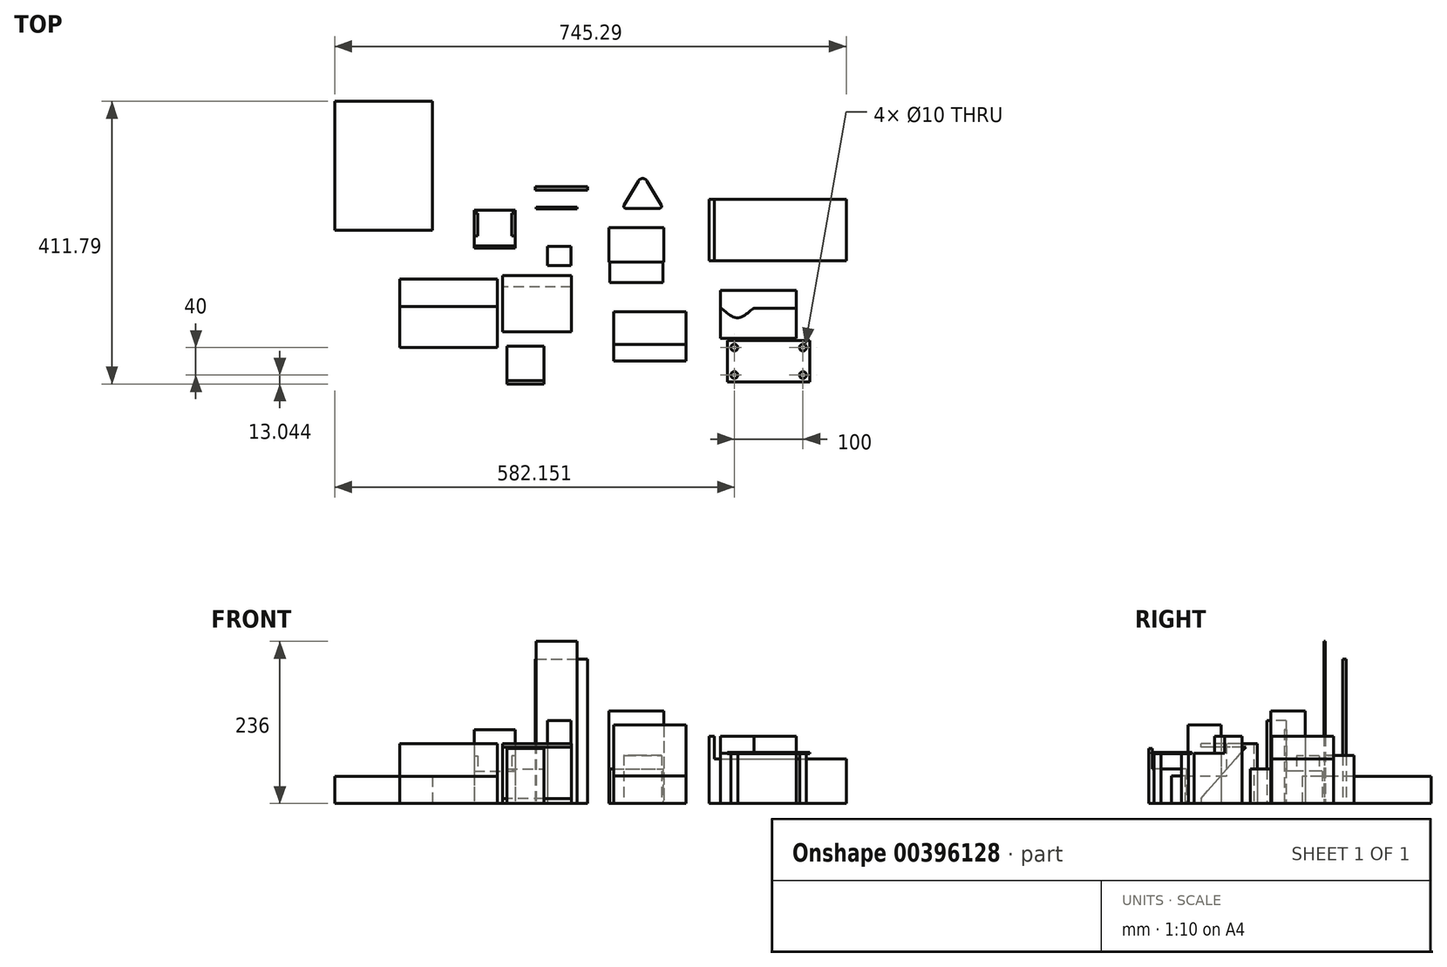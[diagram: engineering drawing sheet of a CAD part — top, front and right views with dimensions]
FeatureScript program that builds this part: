
annotation { "Feature Type Name" : "Feature", "Feature Type Description" : "" }
export const myFeature = defineFeature(function(context is Context, id is Id, definition is map)
    precondition{}
    {
        {
            var Q0;
            Q0=qCreatedBy(makeId("Top.planeOp"),FACE);
            var sketch = newSketch(context, id + "F0", { "sketchPlane" : qUnion([Q0])});
            skLineSegment(sketch, "E0.bottom", {"start": v(-111.36, 82.37) * mm, "end": v(-31.36, 82.37) * mm});
            skLineSegment(sketch, "E0.top", {"start": v(-111.36, 32.37) * mm, "end": v(-31.36, 32.37) * mm});
            skLineSegment(sketch, "E0.left", {"start": v(-111.36, 82.37) * mm, "end": v(-111.36, 32.37) * mm});
            skLineSegment(sketch, "E0.right", {"start": v(-31.36, 82.37) * mm, "end": v(-31.36, 32.37) * mm});
            skLineSegment(sketch, "E1.bottom", {"start": v(34.65, 123.83) * mm, "end": v(234.65, 123.83) * mm});
            skLineSegment(sketch, "E1.top", {"start": v(34.65, 33.83) * mm, "end": v(234.65, 33.83) * mm});
            skLineSegment(sketch, "E1.left", {"start": v(34.65, 123.83) * mm, "end": v(34.65, 33.83) * mm});
            skLineSegment(sketch, "E1.right", {"start": v(234.65, 123.83) * mm, "end": v(234.65, 33.83) * mm});
            skLineSegment(sketch, "E2.bottom", {"start": v(-104.09, -40.21) * mm, "end": v(0.91, -40.21) * mm});
            skLineSegment(sketch, "E2.top", {"start": v(-104.09, -88.21) * mm, "end": v(0.91, -88.21) * mm});
            skLineSegment(sketch, "E2.left", {"start": v(-104.09, -40.21) * mm, "end": v(-104.09, -88.21) * mm});
            skLineSegment(sketch, "E2.right", {"start": v(0.91, -40.21) * mm, "end": v(0.91, -88.21) * mm});
            skLineSegment(sketch, "E3.bottom", {"start": v(51.44, -9.18) * mm, "end": v(161.44, -9.18) * mm});
            skLineSegment(sketch, "E3.top", {"start": v(51.44, -79.18) * mm, "end": v(161.44, -79.18) * mm});
            skLineSegment(sketch, "E3.left", {"start": v(51.44, -9.18) * mm, "end": v(51.44, -79.18) * mm});
            skLineSegment(sketch, "E3.right", {"start": v(161.44, -9.18) * mm, "end": v(161.44, -79.18) * mm});
            skLineSegment(sketch, "E4.bottom", {"start": v(-110.36, 32.37) * mm, "end": v(-32.36, 32.37) * mm});
            skLineSegment(sketch, "E4.top", {"start": v(-110.36, 2.37) * mm, "end": v(-32.36, 2.37) * mm});
            skLineSegment(sketch, "E4.left", {"start": v(-110.36, 32.37) * mm, "end": v(-110.36, 2.37) * mm});
            skLineSegment(sketch, "E4.right", {"start": v(-32.36, 32.37) * mm, "end": v(-32.36, 2.37) * mm});
            skPoint(sketch, "E5", {"position": v(-71.36, 32.37) * mm});
            skPoint(sketch, "E6", {"position": v(-71.36, 2.37) * mm});
            skLineSegment(sketch, "E7", {"start": v(42.4, 123.83) * mm, "end": v(42.4, 33.83) * mm});
            skLineSegment(sketch, "E8.bottom", {"start": v(61.51, -82.45) * mm, "end": v(181.51, -82.45) * mm});
            skLineSegment(sketch, "E8.top", {"start": v(61.51, -142.45) * mm, "end": v(181.51, -142.45) * mm});
            skLineSegment(sketch, "E8.left", {"start": v(61.51, -82.45) * mm, "end": v(61.51, -142.45) * mm});
            skLineSegment(sketch, "E8.right", {"start": v(181.51, -82.45) * mm, "end": v(181.51, -142.45) * mm});
            skCircle(sketch, "E9", {"center": v(71.51, -92.45) * mm, "radius": 5 * mm});
            skCircle(sketch, "E10", {"center": v(71.51, -132.45) * mm, "radius": 5 * mm});
            skCircle(sketch, "E11", {"center": v(171.51, -92.45) * mm, "radius": 5 * mm});
            skCircle(sketch, "E12", {"center": v(171.51, -132.45) * mm, "radius": 5 * mm});
            skLineSegment(sketch, "E13.bottom", {"start": v(-200.88, 54.96) * mm, "end": v(-166.38, 54.96) * mm});
            skLineSegment(sketch, "E13.top", {"start": v(-200.88, 26.96) * mm, "end": v(-166.38, 26.96) * mm});
            skLineSegment(sketch, "E13.left", {"start": v(-200.88, 54.96) * mm, "end": v(-200.88, 26.96) * mm});
            skLineSegment(sketch, "E13.right", {"start": v(-166.38, 54.96) * mm, "end": v(-166.38, 26.96) * mm});
            skLineSegment(sketch, "E14.bottom", {"start": v(-266.16, 12.56) * mm, "end": v(-166.16, 12.56) * mm});
            skLineSegment(sketch, "E14.top", {"start": v(-266.16, -69.44) * mm, "end": v(-166.16, -69.44) * mm});
            skLineSegment(sketch, "E14.left", {"start": v(-266.16, 12.56) * mm, "end": v(-266.16, -69.44) * mm});
            skLineSegment(sketch, "E14.right", {"start": v(-166.16, 12.56) * mm, "end": v(-166.16, -69.44) * mm});
            skLineSegment(sketch, "E15.bottom", {"start": v(-218.52, 142.09) * mm, "end": v(-142.52, 142.09) * mm});
            skLineSegment(sketch, "E15.top", {"start": v(-218.52, 137.09) * mm, "end": v(-142.52, 137.09) * mm});
            skLineSegment(sketch, "E15.left", {"start": v(-218.52, 142.09) * mm, "end": v(-218.52, 137.09) * mm});
            skLineSegment(sketch, "E15.right", {"start": v(-142.52, 142.09) * mm, "end": v(-142.52, 137.09) * mm});
            skLineSegment(sketch, "E16.bottom", {"start": v(-217.4, 111.88) * mm, "end": v(-157.4, 111.88) * mm});
            skLineSegment(sketch, "E16.top", {"start": v(-217.4, 109.88) * mm, "end": v(-157.4, 109.88) * mm});
            skLineSegment(sketch, "E16.left", {"start": v(-217.4, 111.88) * mm, "end": v(-217.4, 109.88) * mm});
            skLineSegment(sketch, "E16.right", {"start": v(-157.4, 111.88) * mm, "end": v(-157.4, 109.88) * mm});
            skLineSegment(sketch, "E17.top", {"start": v(-104.09, -112.21) * mm, "end": v(0.91, -112.21) * mm});
            skLineSegment(sketch, "E17.left", {"start": v(-104.09, -88.21) * mm, "end": v(-104.09, -112.21) * mm});
            skLineSegment(sketch, "E17.right", {"start": v(0.91, -88.21) * mm, "end": v(0.91, -112.21) * mm});
            skLineSegment(sketch, "E18.bottom", {"start": v(-307.61, 107.39) * mm, "end": v(-247.61, 107.39) * mm});
            skLineSegment(sketch, "E18.top", {"start": v(-307.61, 52.39) * mm, "end": v(-247.61, 52.39) * mm});
            skLineSegment(sketch, "E18.left", {"start": v(-307.61, 107.39) * mm, "end": v(-307.61, 52.39) * mm});
            skLineSegment(sketch, "E18.right", {"start": v(-247.61, 107.39) * mm, "end": v(-247.61, 52.39) * mm});
            skLineSegment(sketch, "E19.bottom", {"start": v(-259.82, -90.49) * mm, "end": v(-205.82, -90.49) * mm});
            skLineSegment(sketch, "E19.top", {"start": v(-259.82, -145.49) * mm, "end": v(-205.82, -145.49) * mm});
            skLineSegment(sketch, "E19.left", {"start": v(-259.82, -90.49) * mm, "end": v(-259.82, -145.49) * mm});
            skLineSegment(sketch, "E19.right", {"start": v(-205.82, -90.49) * mm, "end": v(-205.82, -145.49) * mm});
            skLineSegment(sketch, "E20", {"start": v(-62.11, 160.46) * mm, "end": v(-92.11, 110.46) * mm});
            skLineSegment(sketch, "E21", {"start": v(-92.11, 110.46) * mm, "end": v(-32.11, 110.46) * mm});
            skLineSegment(sketch, "E22", {"start": v(-32.11, 110.46) * mm, "end": v(-62.11, 160.46) * mm});
            skPoint(sketch, "E23", {"position": v(-62.11, 110.46) * mm});
            skLineSegment(sketch, "E24.bottom", {"start": v(-415.9, 7.38) * mm, "end": v(-273.9, 7.38) * mm});
            skLineSegment(sketch, "E24.top", {"start": v(-415.9, -92.62) * mm, "end": v(-273.9, -92.62) * mm});
            skLineSegment(sketch, "E24.left", {"start": v(-415.9, 7.38) * mm, "end": v(-415.9, -92.62) * mm});
            skLineSegment(sketch, "E24.right", {"start": v(-273.9, 7.38) * mm, "end": v(-273.9, -92.62) * mm});
            skLineSegment(sketch, "E25.bottom", {"start": v(-510.64, 266.3) * mm, "end": v(-368.64, 266.3) * mm});
            skLineSegment(sketch, "E25.top", {"start": v(-510.64, 78.3) * mm, "end": v(-368.64, 78.3) * mm});
            skLineSegment(sketch, "E25.left", {"start": v(-510.64, 266.3) * mm, "end": v(-510.64, 78.3) * mm});
            skLineSegment(sketch, "E25.right", {"start": v(-368.64, 266.3) * mm, "end": v(-368.64, 78.3) * mm});
            skLineSegment(sketch, "E26.top", {"start": v(-415.9, -32.62) * mm, "end": v(-273.9, -32.62) * mm});
            skLineSegment(sketch, "E26.left", {"start": v(-415.9, 7.38) * mm, "end": v(-415.9, -32.62) * mm});
            skLineSegment(sketch, "E26.right", {"start": v(-273.9, 7.38) * mm, "end": v(-273.9, -32.62) * mm});
            skSolve(sketch);
        }
        {
            var Q0;
            Q0=makeQuery(id+"F0.imprint","IMPRINT",FACE,{"disambiguationData":[TD([[makeQuery(id+"F0.imprint","IMPRINT",EDGE,{"derivedFrom":sQuery(id+"F0.wireOp",EDGE,"E0.bottom")}),-1.0]])]});
            extrude(context, id + "F1", {"entities" : qUnion([Q0]), "depth" : 134.5 * mm});
        }
        {
            var Q0;
            Q0=makeQuery(id+"F0.imprint","IMPRINT",FACE,{"disambiguationData":[TD([[makeQuery(id+"F0.imprint","IMPRINT",EDGE,{"derivedFrom":sQuery(id+"F0.wireOp",EDGE,"E4.top")}),1.0]])]});
            extrude(context, id + "F2", {"entities" : qUnion([Q0]), "operationType" : NewBodyOperationType.ADD, "depth" : 50 * mm});
        }
        {
            var Q0;
            {var subQ2=sQuery(id+"F0.wireOp",EDGE,"E1.right");Q0=makeQuery(id+"F0.imprint","IMPRINT",FACE,{"disambiguationData":[TD([[makeQuery(id+"F0.imprint","IMPRINT",EDGE,{"derivedFrom":subQ2}),-1.0]])]});}
            extrude(context, id + "F3", {"entities" : qUnion([Q0]), "depth" : 65 * mm});
        }
        {
            var Q0;
            {var subQ2=sQuery(id+"F0.wireOp",EDGE,"E1.left");Q0=makeQuery(id+"F0.imprint","IMPRINT",FACE,{"disambiguationData":[TD([[makeQuery(id+"F0.imprint","IMPRINT",EDGE,{"derivedFrom":subQ2}),1.0]])]});}
            extrude(context, id + "F4", {"entities" : qUnion([Q0]), "operationType" : NewBodyOperationType.ADD, "depth" : 98 * mm});
        }
        {
            var Q0;
            Q0=makeQuery(id+"F0.imprint","IMPRINT",FACE,{"disambiguationData":[TD([[makeQuery(id+"F0.imprint","IMPRINT",EDGE,{"derivedFrom":sQuery(id+"F0.wireOp",EDGE,"E3.bottom")}),-1.0]])]});
            extrude(context, id + "F5", {"entities" : qUnion([Q0]), "depth" : 73 * mm});
        }
        {
            var Q0;
            Q0=makeQuery(id+"F0.imprint","IMPRINT",FACE,{"disambiguationData":[TD([[makeQuery(id+"F0.imprint","IMPRINT",EDGE,{"derivedFrom":sQuery(id+"F0.wireOp",EDGE,"E2.bottom")}),-1.0]])]});
            extrude(context, id + "F6", {"entities" : qUnion([Q0]), "depth" : 114 * mm});
        }
        {
            var Q0;
            Q0=makeQuery(id+"F5.opExtrude","CAP_FACE",FACE,{"disambiguationData":[OSD([sQuery(id+"F0.wireOp",EDGE,"E3.bottom"),sQuery(id+"F0.wireOp",EDGE,"E3.top"),sQuery(id+"F0.wireOp",EDGE,"E3.left"),sQuery(id+"F0.wireOp",EDGE,"E3.right")])],"isStart":false});
            var sketch = newSketch(context, id + "F7", { "sketchPlane" : qUnion([Q0])});
            skLineSegment(sketch, "E27", {"start": v(161.44, -35.18) * mm, "end": v(100.44, -35.18) * mm});
            skFitSpline(sketch, "E28", {"points": [v(100.44, -35.18) * mm, v(75.94, -49.18) * mm, v(51.44, -35.18) * mm], "startDerivative": vector(-35.13, -15.5) * mm, "endDerivative": vector(-34.5, 15.56) * mm});
            skSolve(sketch);
        }
        {
            var Q0;
            {var subQ3=sQuery(id+"F7.wireOp",EDGE,"E27");Q0=makeQuery(id+"F7.imprint","IMPRINT",FACE,{"disambiguationData":[TD([[makeQuery(id+"F7.imprint","IMPRINT",EDGE,{"derivedFrom":subQ3}),-1.0]])]});}
            extrude(context, id + "F8", {"entities" : qUnion([Q0]), "operationType" : NewBodyOperationType.ADD, "depth" : 25 * mm});
        }
        {
            var Q0;
            Q0=makeQuery(id+"F0.imprint","IMPRINT",FACE,{"disambiguationData":[TD([[makeQuery(id+"F0.imprint","IMPRINT",EDGE,{"derivedFrom":sQuery(id+"F0.wireOp",EDGE,"E9")}),1.0]])]});
            var Q1;
            Q1=makeQuery(id+"F0.imprint","IMPRINT",FACE,{"disambiguationData":[TD([[makeQuery(id+"F0.imprint","IMPRINT",EDGE,{"derivedFrom":sQuery(id+"F0.wireOp",EDGE,"E11")}),1.0]])]});
            var Q2;
            Q2=makeQuery(id+"F0.imprint","IMPRINT",FACE,{"disambiguationData":[TD([[makeQuery(id+"F0.imprint","IMPRINT",EDGE,{"derivedFrom":sQuery(id+"F0.wireOp",EDGE,"E12")}),1.0]])]});
            var Q3;
            Q3=makeQuery(id+"F0.imprint","IMPRINT",FACE,{"disambiguationData":[TD([[makeQuery(id+"F0.imprint","IMPRINT",EDGE,{"derivedFrom":sQuery(id+"F0.wireOp",EDGE,"E10")}),1.0]])]});
            extrude(context, id + "F9", {"entities" : qUnion([Q0, Q1, Q2, Q3]), "depth" : 74 * mm});
        }
        {
            var Q0;
            Q0=makeQuery(id+"F0.imprint","IMPRINT",FACE,{"disambiguationData":[TD([[makeQuery(id+"F0.imprint","IMPRINT",EDGE,{"derivedFrom":sQuery(id+"F0.wireOp",EDGE,"E8.bottom")}),-1.0]])]});
            extrude(context, id + "F10", {"entities" : qUnion([Q0]), "depth" : 74 * mm, "hasSecondDirection" : true, "secondDirectionOppositeDirection" : false, "secondDirectionDepth" : 72 * mm});
        }
        {
            var Q0;
            Q0=makeQuery(id+"F0.imprint","IMPRINT",FACE,{"disambiguationData":[TD([[makeQuery(id+"F0.imprint","IMPRINT",EDGE,{"derivedFrom":sQuery(id+"F0.wireOp",EDGE,"E13.bottom")}),-1.0]])]});
            extrude(context, id + "F11", {"entities" : qUnion([Q0]), "depth" : 120.5 * mm, "offsetDistance" : 25 * mm});
        }
        {
            var Q0;
            Q0=makeQuery(id+"F0.imprint","IMPRINT",FACE,{"disambiguationData":[TD([[makeQuery(id+"F0.imprint","IMPRINT",EDGE,{"derivedFrom":sQuery(id+"F0.wireOp",EDGE,"E14.bottom")}),-1.0]])]});
            extrude(context, id + "F12", {"entities" : qUnion([Q0]), "depth" : 87 * mm, "offsetDistance" : 25 * mm});
        }
        {
            var Q0;
            Q0=makeQuery(id+"F0.imprint","IMPRINT",FACE,{"disambiguationData":[TD([[makeQuery(id+"F0.imprint","IMPRINT",EDGE,{"derivedFrom":sQuery(id+"F0.wireOp",EDGE,"E15.bottom")}),-1.0]])]});
            extrude(context, id + "F13", {"entities" : qUnion([Q0]), "depth" : 210 * mm, "offsetDistance" : 25 * mm});
        }
        {
            var Q0;
            Q0=makeQuery(id+"F0.imprint","IMPRINT",FACE,{"disambiguationData":[TD([[makeQuery(id+"F0.imprint","IMPRINT",EDGE,{"derivedFrom":sQuery(id+"F0.wireOp",EDGE,"E16.bottom")}),-1.0]])]});
            extrude(context, id + "F14", {"entities" : qUnion([Q0]), "depth" : 236 * mm, "offsetDistance" : 25 * mm});
        }
        {
            var Q0;
            Q0=makeQuery(id+"F0.imprint","IMPRINT",FACE,{"disambiguationData":[TD([[makeQuery(id+"F0.imprint","IMPRINT",EDGE,{"derivedFrom":sQuery(id+"F0.wireOp",EDGE,"E2.top")}),-1.0]])]});
            extrude(context, id + "F15", {"entities" : qUnion([Q0]), "operationType" : NewBodyOperationType.ADD, "depth" : 40 * mm, "offsetDistance" : 25 * mm});
        }
        {
            var Q0;
            Q0=makeQuery(id+"F12.opExtrude","CAP_EDGE",EDGE,{"disambiguationData":[OSD([sQuery(id+"F0.wireOp",EDGE,"E14.top")])],"isStart":false});
            chamfer(context, id + "F16", {"entities" : qUnion([Q0]), "chamferType" : ChamferType.TWO_OFFSETS, "width1" : 70 * mm, "oppositeDirection" : false, "width2" : 80 * mm, "tangentPropagation" : true});
        }
        {
            var Q0;
            Q0=makeQuery(id+"F12.opExtrude","CAP_FACE",FACE,{"disambiguationData":[OSD([sQuery(id+"F0.wireOp",EDGE,"E14.bottom"),sQuery(id+"F0.wireOp",EDGE,"E14.top"),sQuery(id+"F0.wireOp",EDGE,"E14.left"),sQuery(id+"F0.wireOp",EDGE,"E14.right")])],"isStart":false});
            var sketch = newSketch(context, id + "F17", { "sketchPlane" : qUnion([Q0])});
            skPoint(sketch, "E29.oppositeSnap0", {"position": v(-166.16, 6.56) * mm});
            skLineSegment(sketch, "E29.bottom", {"start": v(-266.16, 12.56) * mm, "end": v(-166.16, 12.56) * mm});
            skLineSegment(sketch, "E29.top", {"start": v(-266.16, -69.44) * mm, "end": v(-166.16, -69.44) * mm});
            skLineSegment(sketch, "E29.left", {"start": v(-266.16, 12.56) * mm, "end": v(-266.16, -69.44) * mm});
            skLineSegment(sketch, "E29.right", {"start": v(-166.16, 12.56) * mm, "end": v(-166.16, -69.44) * mm});
            skSolve(sketch);
        }
        {
            var Q0;
            {var subQ0=sQuery(id+"F17.wireOp",EDGE,"E29.top");Q0=makeQuery(id+"F17.imprint","IMPRINT",FACE,{"disambiguationData":[TD([[makeQuery(id+"F17.imprint","IMPRINT",EDGE,{"derivedFrom":subQ0}),1.0]])]});}
            var Q1;
            {var subQ0=sQuery(id+"F17.wireOp",EDGE,"E29.bottom");Q1=makeQuery(id+"F17.imprint","IMPRINT",FACE,{"disambiguationData":[TD([[makeQuery(id+"F17.imprint","IMPRINT",EDGE,{"derivedFrom":subQ0}),-1.0]])]});}
            extrude(context, id + "F18", {"entities" : qUnion([Q0, Q1]), "operationType" : NewBodyOperationType.ADD, "oppositeDirection" : true, "depth" : 5 * mm, "offsetDistance" : 25 * mm});
        }
        {
            var Q0;
            Q0=makeQuery(id+"F0.imprint","IMPRINT",FACE,{"disambiguationData":[TD([[makeQuery(id+"F0.imprint","IMPRINT",EDGE,{"derivedFrom":sQuery(id+"F0.wireOp",EDGE,"E18.bottom")}),-1.0]])]});
            extrude(context, id + "F19", {"entities" : qUnion([Q0]), "depth" : 47 * mm, "offsetDistance" : 25 * mm});
        }
        {
            var Q0;
            Q0=makeQuery(id+"F0.imprint","IMPRINT",FACE,{"disambiguationData":[TD([[makeQuery(id+"F0.imprint","IMPRINT",EDGE,{"derivedFrom":sQuery(id+"F0.wireOp",EDGE,"E19.bottom")}),-1.0]])]});
            extrude(context, id + "F20", {"entities" : qUnion([Q0]), "depth" : 50 * mm, "offsetDistance" : 25 * mm});
        }
        {
            var Q0;
            Q0=makeQuery(id+"F19.opExtrude","CAP_FACE",FACE,{"disambiguationData":[OSD([sQuery(id+"F0.wireOp",EDGE,"E18.bottom"),sQuery(id+"F0.wireOp",EDGE,"E18.top"),sQuery(id+"F0.wireOp",EDGE,"E18.left"),sQuery(id+"F0.wireOp",EDGE,"E18.right")])],"isStart":false});
            var sketch = newSketch(context, id + "F21", { "sketchPlane" : qUnion([Q0])});
            skLineSegment(sketch, "E30.bottom", {"start": v(-307.61, 103.04) * mm, "end": v(-302.61, 103.04) * mm});
            skLineSegment(sketch, "E30.top", {"start": v(-307.61, 70.04) * mm, "end": v(-302.61, 70.04) * mm});
            skLineSegment(sketch, "E30.left", {"start": v(-307.61, 103.04) * mm, "end": v(-307.61, 70.04) * mm});
            skLineSegment(sketch, "E30.right", {"start": v(-302.61, 103.04) * mm, "end": v(-302.61, 70.04) * mm});
            skLineSegment(sketch, "E31.bottom", {"start": v(-247.61, 103.04) * mm, "end": v(-252.61, 103.04) * mm});
            skLineSegment(sketch, "E31.top", {"start": v(-247.61, 70.04) * mm, "end": v(-252.61, 70.04) * mm});
            skLineSegment(sketch, "E31.left", {"start": v(-247.61, 103.04) * mm, "end": v(-247.61, 70.04) * mm});
            skLineSegment(sketch, "E31.right", {"start": v(-252.61, 103.04) * mm, "end": v(-252.61, 70.04) * mm});
            skLineSegment(sketch, "E32.bottom", {"start": v(-307.61, 55.39) * mm, "end": v(-247.61, 55.39) * mm});
            skLineSegment(sketch, "E32.top", {"start": v(-307.61, 52.39) * mm, "end": v(-247.61, 52.39) * mm});
            skLineSegment(sketch, "E32.left", {"start": v(-307.61, 55.39) * mm, "end": v(-307.61, 52.39) * mm});
            skLineSegment(sketch, "E32.right", {"start": v(-247.61, 55.39) * mm, "end": v(-247.61, 52.39) * mm});
            skSolve(sketch);
        }
        {
            var Q0;
            Q0=makeQuery(id+"F21.imprint","IMPRINT",FACE,{"disambiguationData":[TD([[makeQuery(id+"F21.imprint","IMPRINT",EDGE,{"derivedFrom":sQuery(id+"F21.wireOp",EDGE,"E30.bottom")}),-1.0]])]});
            var Q1;
            Q1=makeQuery(id+"F21.imprint","IMPRINT",FACE,{"disambiguationData":[TD([[makeQuery(id+"F21.imprint","IMPRINT",EDGE,{"derivedFrom":sQuery(id+"F21.wireOp",EDGE,"E31.bottom")}),1.0]])]});
            extrude(context, id + "F22", {"entities" : qUnion([Q0, Q1]), "operationType" : NewBodyOperationType.ADD, "depth" : 22 * mm, "offsetDistance" : 25 * mm});
        }
        {
            var Q0;
            Q0=makeQuery(id+"F21.imprint","IMPRINT",FACE,{"disambiguationData":[TD([[makeQuery(id+"F21.imprint","IMPRINT",EDGE,{"derivedFrom":sQuery(id+"F21.wireOp",EDGE,"E32.bottom")}),-1.0]])]});
            extrude(context, id + "F23", {"entities" : qUnion([Q0]), "operationType" : NewBodyOperationType.ADD, "depth" : 60 * mm, "offsetDistance" : 25 * mm});
        }
        {
            var Q0;
            Q0=makeQuery(id+"F20.opExtrude","CAP_FACE",FACE,{"disambiguationData":[OSD([sQuery(id+"F0.wireOp",EDGE,"E19.bottom"),sQuery(id+"F0.wireOp",EDGE,"E19.top"),sQuery(id+"F0.wireOp",EDGE,"E19.left"),sQuery(id+"F0.wireOp",EDGE,"E19.right")])],"isStart":false});
            var sketch = newSketch(context, id + "F24", { "sketchPlane" : qUnion([Q0])});
            skLineSegment(sketch, "E33.bottom", {"start": v(-259.82, -145.49) * mm, "end": v(-205.82, -145.49) * mm});
            skLineSegment(sketch, "E33.top", {"start": v(-259.82, -140.49) * mm, "end": v(-205.82, -140.49) * mm});
            skLineSegment(sketch, "E33.left", {"start": v(-259.82, -145.49) * mm, "end": v(-259.82, -140.49) * mm});
            skLineSegment(sketch, "E33.right", {"start": v(-205.82, -145.49) * mm, "end": v(-205.82, -140.49) * mm});
            skSolve(sketch);
        }
        {
            var Q0;
            Q0=makeQuery(id+"F24.imprint","IMPRINT",FACE,{"disambiguationData":[TD([[makeQuery(id+"F24.imprint","IMPRINT",EDGE,{"derivedFrom":sQuery(id+"F24.wireOp",EDGE,"E33.bottom")}),1.0]])]});
            extrude(context, id + "F25", {"entities" : qUnion([Q0]), "operationType" : NewBodyOperationType.ADD, "depth" : 30 * mm, "offsetDistance" : 25 * mm});
        }
        {
            var Q0;
            Q0=makeQuery(id+"F0.imprint","IMPRINT",FACE,{"disambiguationData":[TD([[makeQuery(id+"F0.imprint","IMPRINT",EDGE,{"derivedFrom":sQuery(id+"F0.wireOp",EDGE,"E20")}),1.0]])]});
            extrude(context, id + "F26", {"entities" : qUnion([Q0]), "depth" : 70 * mm, "offsetDistance" : 25 * mm});
        }
        {
            var Q0;
            Q0=makeQuery(id+"F26.opExtrude","SWEPT_EDGE",EDGE,{"disambiguationData":[OSD([sQuery(id+"F0.wireOp",EDGE,"E20"),sQuery(id+"F0.wireOp",EDGE,"E21")])]});
            var Q1;
            Q1=makeQuery(id+"F26.opExtrude","SWEPT_EDGE",EDGE,{"disambiguationData":[OSD([sQuery(id+"F0.wireOp",EDGE,"E21"),sQuery(id+"F0.wireOp",EDGE,"E22")])]});
            fillet(context, id + "F27", {"entities" : qUnion([Q0, Q1]), "radius" : 3 * mm, "tangentPropagation" : true, "allowEdgeOverflow" : false});
        }
        {
            var Q0;
            Q0=makeQuery(id+"F26.opExtrude","SWEPT_EDGE",EDGE,{"disambiguationData":[OSD([sQuery(id+"F0.wireOp",EDGE,"E20"),sQuery(id+"F0.wireOp",EDGE,"E22")])]});
            fillet(context, id + "F28", {"entities" : qUnion([Q0]), "radius" : 7 * mm, "tangentPropagation" : true, "allowEdgeOverflow" : false});
        }
        {
            var Q0;
            {var subQ0=sQuery(id+"F0.wireOp",EDGE,"E24.top");Q0=makeQuery(id+"F0.imprint","IMPRINT",FACE,{"disambiguationData":[TD([[makeQuery(id+"F0.imprint","IMPRINT",EDGE,{"derivedFrom":subQ0}),1.0]])]});}
            var Q1;
            Q1=makeQuery(id+"F0.imprint","IMPRINT",FACE,{"disambiguationData":[TD([[makeQuery(id+"F0.imprint","IMPRINT",EDGE,{"derivedFrom":sQuery(id+"F0.wireOp",EDGE,"E25.bottom")}),-1.0]])]});
            extrude(context, id + "F29", {"entities" : qUnion([Q0, Q1]), "depth" : 39 * mm, "offsetDistance" : 25 * mm});
        }
        {
            var Q0;
            {var subQ0=sQuery(id+"F0.wireOp",EDGE,"E24.bottom");Q0=makeQuery(id+"F0.imprint","IMPRINT",FACE,{"disambiguationData":[TD([[makeQuery(id+"F0.imprint","IMPRINT",EDGE,{"derivedFrom":subQ0}),-1.0]])]});}
            extrude(context, id + "F30", {"entities" : qUnion([Q0]), "operationType" : NewBodyOperationType.ADD, "depth" : 87 * mm, "offsetDistance" : 25 * mm});
        }
    });
